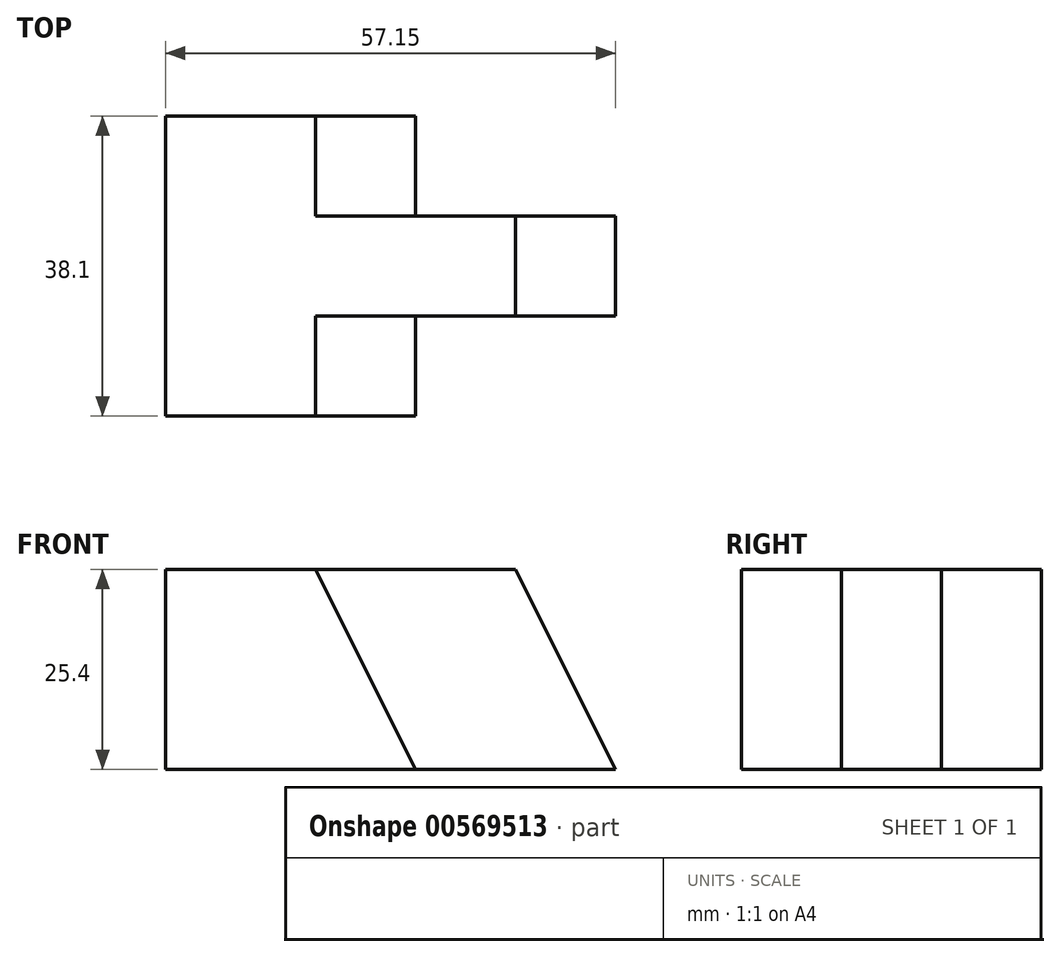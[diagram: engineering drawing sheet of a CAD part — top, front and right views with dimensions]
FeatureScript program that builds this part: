
annotation { "Feature Type Name" : "Feature", "Feature Type Description" : "" }
export const myFeature = defineFeature(function(context is Context, id is Id, definition is map)
    precondition{}
    {
        {
            var Q0;
            Q0=qCreatedBy(makeId("Top.planeOp"),FACE);
            var sketch = newSketch(context, id + "F0", { "sketchPlane" : qUnion([Q0])});
            skLineSegment(sketch, "E0", {"start": v(-65.14, 50.3) * mm, "end": v(-65.14, 12.2) * mm});
            skLineSegment(sketch, "E1", {"start": v(-65.14, 12.2) * mm, "end": v(-7.99, 12.2) * mm});
            skLineSegment(sketch, "E2", {"start": v(-7.99, 12.2) * mm, "end": v(-7.99, 50.3) * mm});
            skLineSegment(sketch, "E3", {"start": v(-7.99, 50.3) * mm, "end": v(-65.14, 50.3) * mm});
            skSolve(sketch);
        }
        {
            var Q0;
            Q0=makeQuery(id+"F0.imprint","IMPRINT",FACE,{"disambiguationData":[TD([[makeQuery(id+"F0.imprint","IMPRINT",EDGE,{"derivedFrom":sQuery(id+"F0.wireOp",EDGE,"E0")}),1.0]])]});
            extrude(context, id + "F1", {"entities" : qUnion([Q0]), "depth" : 25.4 * mm, "offsetDistance" : 25.4 * mm});
        }
        {
            var Q0;
            Q0=makeQuery(id+"F1.opExtrude","SWEPT_FACE",FACE,{"disambiguationData":[OSD([sQuery(id+"F0.wireOp",EDGE,"E1")])]});
            var sketch = newSketch(context, id + "F2", { "sketchPlane" : qUnion([Q0])});
            skLineSegment(sketch, "E4", {"start": v(-46.09, 25.4) * mm, "end": v(-33.39, 0) * mm});
            skLineSegment(sketch, "E5", {"start": v(-33.39, 0) * mm, "end": v(-7.99, 0) * mm});
            skLineSegment(sketch, "E6", {"start": v(-7.99, 0) * mm, "end": v(-7.99, 25.4) * mm});
            skLineSegment(sketch, "E7", {"start": v(-7.99, 25.4) * mm, "end": v(-46.09, 25.4) * mm});
            skSolve(sketch);
        }
        {
            var Q0;
            Q0=makeQuery(id+"F2.imprint","IMPRINT",FACE,{"disambiguationData":[TD([[makeQuery(id+"F2.imprint","IMPRINT",EDGE,{"derivedFrom":sQuery(id+"F2.wireOp",EDGE,"E4")}),1.0]])]});
            extrude(context, id + "F3", {"entities" : qUnion([Q0]), "operationType" : NewBodyOperationType.REMOVE, "oppositeDirection" : true, "depth" : 12.7 * mm, "offsetDistance" : 25.4 * mm});
        }
        {
            var Q0;
            Q0=makeQuery(id+"F1.opExtrude","SWEPT_FACE",FACE,{"disambiguationData":[OSD([sQuery(id+"F0.wireOp",EDGE,"E3")])]});
            var sketch = newSketch(context, id + "F4", { "sketchPlane" : qUnion([Q0])});
            skLineSegment(sketch, "E8", {"start": v(46.09, 25.4) * mm, "end": v(7.99, 25.4) * mm});
            skLineSegment(sketch, "E9", {"start": v(7.99, 25.4) * mm, "end": v(7.99, 0) * mm});
            skLineSegment(sketch, "E10", {"start": v(7.99, 0) * mm, "end": v(33.39, 0) * mm});
            skLineSegment(sketch, "E11", {"start": v(33.39, 0) * mm, "end": v(46.09, 25.4) * mm});
            skSolve(sketch);
        }
        {
            var Q0;
            Q0 = qSketchRegion(id + "F4", true);
            extrude(context, id + "F5", {"entities" : qUnion([Q0]), "operationType" : NewBodyOperationType.REMOVE, "oppositeDirection" : true, "depth" : 12.7 * mm, "offsetDistance" : 25.4 * mm});
        }
        {
            var Q0;
            Q0=makeQuery(id+"F3.boolean.opBoolean","COPY",FACE,{"derivedFrom":makeQuery(id+"F3.opExtrude","CAP_FACE",FACE,{"disambiguationData":[OSD([sQuery(id+"F2.wireOp",EDGE,"E4"),sQuery(id+"F2.wireOp",EDGE,"E5"),sQuery(id+"F2.wireOp",EDGE,"E6"),sQuery(id+"F2.wireOp",EDGE,"E7")])],"isStart":false})});
            var sketch = newSketch(context, id + "F6", { "sketchPlane" : qUnion([Q0])});
            skLineSegment(sketch, "E12", {"start": v(-20.69, 25.4) * mm, "end": v(-7.99, 25.4) * mm});
            skLineSegment(sketch, "E13", {"start": v(-7.99, 25.4) * mm, "end": v(-7.99, 0) * mm});
            skLineSegment(sketch, "E14", {"start": v(-7.99, 0) * mm, "end": v(-20.69, 25.4) * mm});
            skSolve(sketch);
        }
        {
            var Q0;
            Q0 = qSketchRegion(id + "F6", true);
            extrude(context, id + "F7", {"entities" : qUnion([Q0]), "operationType" : NewBodyOperationType.REMOVE, "oppositeDirection" : true, "depth" : 12.7 * mm, "offsetDistance" : 25.4 * mm});
        }
    });
